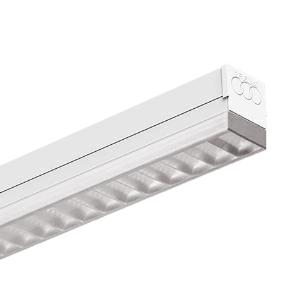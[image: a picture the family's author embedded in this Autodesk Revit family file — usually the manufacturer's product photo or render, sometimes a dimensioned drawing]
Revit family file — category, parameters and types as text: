
# Revit family: 3f_filippi_-_3f_zeta_dr_ugr_3f_filippi_-_11004_-_3f_zeta_dr_ugr_2x22-940_led_dali_l1783
name_source: partatom
category: Lighting Fixtures
units: mm (PartAtom-declared; Revit-internal decimal feet)

## family parameters
Cut with Voids When Loaded = No
Host = Face
Light Source = No
Part Type = Normal
Room Calculation Point = No
Round Connector Dimension = Use Diameter
Shared = No

## types (1)
- 3F Filippi - 3F Zeta DR UGR (1 x LED, 4155 lm, 49 W, 4000 K)
    Apparent Load = 49 VA
    Approval mark = CE
    CIE Flux Codes = 71 97 100 99 100
    Color Rendering = 90
    Color Temperature = 4000 K
    Control Gear = Electronic transformer
    Default Elevation = 1800 mm
    Description = ILLUMINOTECHNICAL
Luminous efficiency 100% (DLOR 99%, ULOR 1%).
Initial luminous flux of the luminaire 4155 lm.
Controlled direct symmetric distribution.
Installation Interdistance Transv.D = 1.30 x hu - Long.D = 1.20 x hu.
Average luminance <3000 cd/m² for radial angles >65°.
Tabular UGR (CIE 117 - 4H-8H; S=0.25H; 70/50/20): RUG 16.9 - 18.2.
Beam angle: 87° - 90°.
Luminous efficacy 85 lm/W.
Lifetime (L93/B10): 30000 h. (tq+25°C)
Lifetime (L90/B10): 50000 h. (tq+25°C)
Lifetime (L85/B10): 80000 h. (tq+25°C)
Lifetime (L80/B10): 100000 h. (tq+25°C)
Sudden decreased luminous flux after 50000 hours: 0% (C0).
Photobiological safety in compliance with IEC/TR 62778: RG0 risk exempt, (IEC 62471).
In compliance with IEC/EN 62722-2-1 - IEC/EN 62717 standards.

SOURCE
2 linear LED modules 22W/940.
Energy efficiency class (UE 2019/2020 - UE 2019/2015): E.
CIE 13.3 Colour rendering index: CRI >90 (R9 >50%).
IES TM-30 Fidelity Index: Rf = 92 Rg = 101.
CCT nominal colour temperature 4000 K.
Colour initial tolerance (MacAdam): SDCM 3.

MECHANICAL
Housing in hot-galvanised steel, painted in white polyester, obtained through rolling process.
Light unit in hot-galvanised steel, painted in white polyester base with fixing springs and retractable safety hooks in stainless steel.
Semi-specular aluminium internal louvre with prismatic methacrylate (PMMA) filter above the louvre blades for complete shielding of the louvre compartment.
Rectangular screen in self-extinguishing polycarbonate, UV stabilised, transparent, with smooth outer surface.
End caps in white polycarbonate.
Pair of stainless steel sliding brackets with sliding block screws.
Luminaire with limited surface temperature. - D - (EN 60598-2-24)
Dimensions: 1783x62 mm, height 81 mm. Weight 5.2 kg.
IP40 protection degree.
Mechanical strength to impacts IK06 (1 joule).
Glow-wire test resistance 850°C.

ELECTRICAL
Halogen Free DALI-2 DATI (Parts 251, 252, 253), PUSH-DIM, electronic wiring 230V-50/60Hz, power factor 0.95 at full load, THD <25%, constant output current, SELV, class I, 1 driver, 1 DALI addresse.
Power of the luminaire 49 W.
ENEC - CE.
SAFE FLICKER: PstLM=<1 and SVM=<0.4 (IEC TR 61547-1 and IEC TR 63158), to ensure a more comfortable and safe light.
Luminaire compliant with EN 60598-2-22 for power supply from a centralised emergency system CPSS (Central Power Supply System), not incorporated in the luminaire - high risk areas excluded. The default power and flux are 100% in AC and 15% in DC.
Ambient temperature from 0°C to +25°C.
Temperature class T6 max 85°C.
Relative humidity UR: <85%.

INSTALLATION
Ceiling / Suspended / Wall.
All accessories dedicated to this product are available on the Catalog and on our website www.3F-Filippi.com.

APPLICATIONS
Suitable product for food production plants (HACCP), IFS (Food Version 6), BRC (GSFS Food Version 7).
In environments with VDTs, managerial offices and staterooms, public offices and schools.

LIGHT MANAGEMENT
Recommended minimum setting: 10%.
The luminaire, equipped with (DALI-2 DATI) driver, can be controlled manually with 3F Easy Dim technology or automatically/manually with wired or wireless DALI/D2D control systems.
The D2D driver guarantees interoperability with other devices with the same certification by making the following information available:
Device Data (Part 251), Energy Report (Part 252), Diagnosis & Maintenance (Part 253).
In electrical systems without a regulation system (manual or automatic) and DALI bus, a suitable jumper must be made on the DA-DA terminals of the appliance.

WARNING
Luminaire designed for disposal/recycling at end-of-life.
Replaceable (LED only) light source by a professional. Replaceable control gear by a professional.
    Height = 81 mm
    Lamp = 1 x LED
    Lamp Light Flux = 4155 lm
    Lamp Power = 49 W
    Lamp count = 1
    Length = 1783 mm
    Lifetime = 50000 h
    Luminous efficacy = 85 lm/W
    Manufacturer = 3F Filippi
    ModVariant = No
    Model = 3F Filippi - 11004 - 3F Zeta DR UGR 2x22-940 LED DALI L1783
    Mounting Place = Ceiling
    Mounting Type = Surface mounted
    Number of Poles = 1
    OnlyDefault = Yes
    Power Factor = 1
    Product Name = 3F Filippi - 3F Zeta DR UGR
    Product group = ceiling mounted luminaire
    ProductGroupID = 3
    Protection Class = Protection class I
    Protection Degree = IP 40
    RLX_Detail_Level = 1
    RLX_Emergency_Light_Flux = 0 lm
    RLX_Emergency_Type = 0
    RLX_Emergency_Type_DB = No
    RlxData = <blob elided: 50089 chars, md5=5db93373>
    Socket = socket
    Standby Power = 0 W
    System Light Flux = 4155 lm
    System Power = 49 W
    Type Comments = Product without accessories
    Type Image = 3ffilippi_3f_zeta_dr_ugr.jpg
    URL = http://relux.com
    VarID = ---
    Voltage = 0 V
    Weight = 0.00 kg
    Width = 62 mm  [stored 0.203412 ft]

note: [stored X ft] marks values corroborated as IEEE doubles in the binary element streams (Revit-internal decimal feet)

## geometry (parser evidence)
native form markers: Blend x4, Sweep x11
no freeform markers — native parametric forms only
